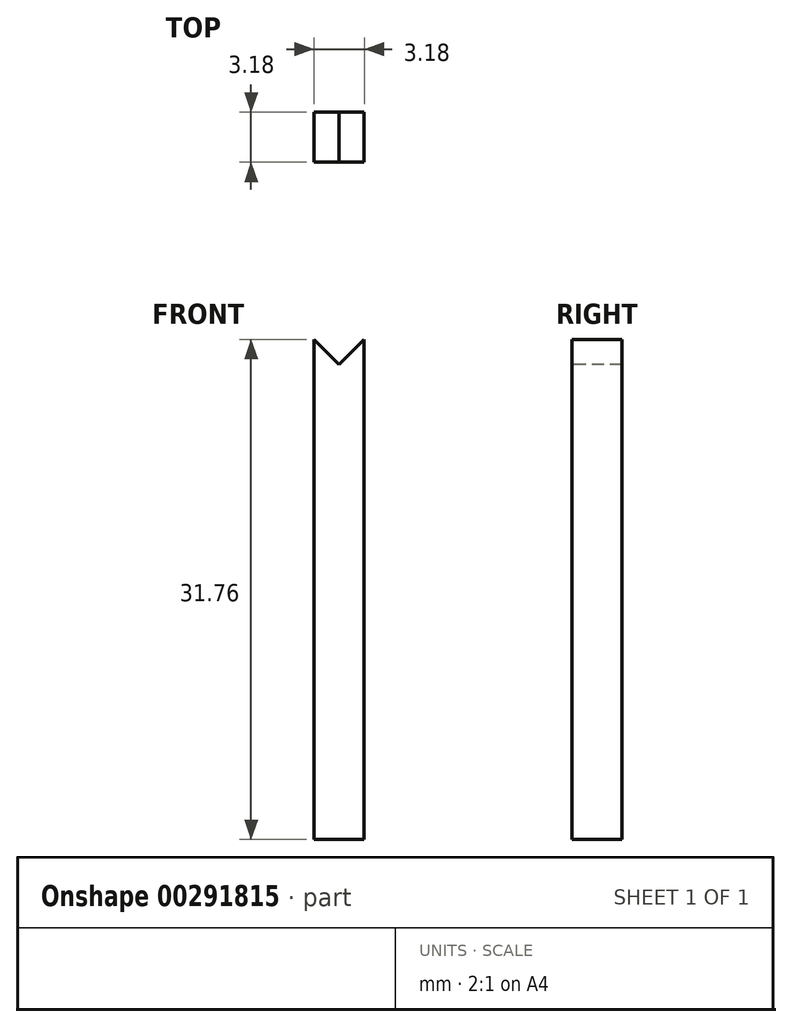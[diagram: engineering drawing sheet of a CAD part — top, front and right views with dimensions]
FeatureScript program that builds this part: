
annotation { "Feature Type Name" : "Feature", "Feature Type Description" : "" }
export const myFeature = defineFeature(function(context is Context, id is Id, definition is map)
    precondition{}
    {
        {
            var Q0;
            Q0=qCreatedBy(makeId("Front.planeOp"),FACE);
            var sketch = newSketch(context, id + "F0", { "sketchPlane" : qUnion([Q0])});
            skLineSegment(sketch, "E0.bottom", {"start": v(1.59, 15.88) * mm, "end": v(-1.59, 15.88) * mm});
            skLineSegment(sketch, "E0.top", {"start": v(1.59, -15.88) * mm, "end": v(-1.59, -15.88) * mm});
            skLineSegment(sketch, "E0.left", {"start": v(1.59, 15.88) * mm, "end": v(1.59, -15.88) * mm});
            skLineSegment(sketch, "E0.right", {"start": v(-1.59, 15.88) * mm, "end": v(-1.59, -15.88) * mm});
            skPoint(sketch, "E0.middle", {"position": v(0, 0) * mm});
            skSolve(sketch);
        }
        {
            var Q0;
            Q0 = qSketchRegion(id + "F0", true);
            extrude(context, id + "F1", {"entities" : qUnion([Q0]), "endBound" : BoundingType.SYMMETRIC, "depth" : 3.17 * mm});
        }
        {
            var Q0;
            Q0=makeQuery(id+"F1.opExtrude","CAP_FACE",FACE,{"disambiguationData":[OSD([sQuery(id+"F0.wireOp",EDGE,"E0.bottom"),sQuery(id+"F0.wireOp",EDGE,"E0.top"),sQuery(id+"F0.wireOp",EDGE,"E0.left"),sQuery(id+"F0.wireOp",EDGE,"E0.right")])],"isStart":false});
            var sketch = newSketch(context, id + "F2", { "sketchPlane" : qUnion([Q0])});
            skLineSegment(sketch, "E1", {"start": v(-1.59, 15.88) * mm, "end": v(0, 14.29) * mm});
            skLineSegment(sketch, "E2", {"start": v(0, 14.29) * mm, "end": v(1.59, 15.87) * mm});
            skLineSegment(sketch, "E3", {"start": v(-1.59, 15.88) * mm, "end": v(1.59, 15.88) * mm});
            skSolve(sketch);
        }
        {
            var Q0;
            Q0 = qSketchRegion(id + "F2", true);
            extrude(context, id + "F3", {"entities" : qUnion([Q0]), "operationType" : NewBodyOperationType.REMOVE, "endBound" : BoundingType.THROUGH_ALL, "oppositeDirection" : true, "depth" : 25.4 * mm});
        }
    });
